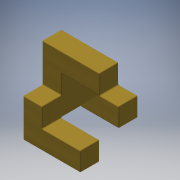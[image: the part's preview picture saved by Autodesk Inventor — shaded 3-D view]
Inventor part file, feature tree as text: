
AUTODESK INVENTOR PART (.ipt)
format: ipt  version: 2016 (Build 200138000, 138)  size: 217,600 bytes
history: native  units: in
note: dims shown in document units (in); Inventor stores cm internally (conversion verified against a paired STEP export)
features: plane x8, extrude x4, other x1, fillet x1, sketch x1
ambient origin geometry x8: Origin, YZ Plane, XZ Plane, XY Plane, X Axis, Y Axis, Z Axis, Center Point
bodies: Solid1 (feature_tree)
feature tree (15):
  other  "Cube Master.ipt"
  extrude  "Extrusion1"  Depth=0.0193in TaperAngle=0.0deg
  extrude  "Extrusion2"  Depth=0.0193in TaperAngle=0.0deg
  extrude  "Extrusion3"  Depth=0.0193in TaperAngle=0.0deg
  extrude  "Extrusion4"  Depth=0.0193in TaperAngle=0.0deg
  fillet  "Fillet1"  Radius=0.0193in
  sketch  "Sketch1"  dims[d0=0.3937in d1=1.0in d2=0.0in d3=1.0in d4=0.0in d5=1.0in d6=0.0in d7=1.0in d8=0.0in d10=0.0193in d11=0.0193in]
  plane  "Work Plane1"
  plane  "Work Plane2"
  plane  "Work Plane3"
  plane  "Work Plane4"
  plane  "Work Plane5"
  plane  "Work Plane6"
  plane  "Work Plane7"
  plane  "Work Plane8"
